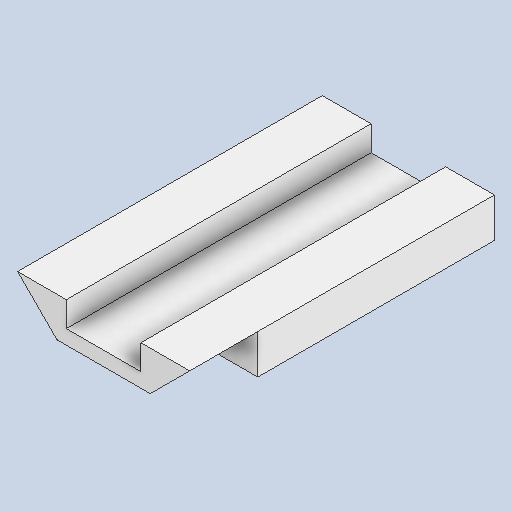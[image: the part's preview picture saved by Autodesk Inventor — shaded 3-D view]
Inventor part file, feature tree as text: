
AUTODESK INVENTOR PART (.ipt)
format: ipt  version: 2023 (Build 270158000, 158)  size: 268,800 bytes
history: native  units: mm
features: sketch x3, extrude x2, hole x1
ambient origin geometry x8: Origin, YZ Plane, XZ Plane, XY Plane, X Axis, Y Axis, Z Axis, Center Point
bodies: Solid1 (feature_tree)
feature tree (6):
  extrude  "Extrusion1"  TaperAngle=45.0deg  [1 undecoded]
  extrude  "Extrusion2"  Depth=10.4mm
  hole  "Hole1"  [1 undecoded]
  sketch  "Sketch1"  dims[d0=45.0deg d1=45.0deg]
  sketch  "Sketch2"  dims[d2=2.0mm d3=10.4mm]
  sketch  "Sketch3"  dims[d4=3.5mm d6=24.0mm d7=9.5mm d8=0.0mm d9=33.0mm d10=0.0mm d11=2.2mm d12=6.0mm d13=4.0mm d14=2.0mm d15=90.0deg d16=2.5mm d17=0.0mm d18=15.4mm d20=3.8mm d21=1.3mm]
note: 2 required parameter values undecoded (feature->parameter linkage not recoverable at this tier; creation-order binding heuristic only, values carry confidence <= 0.55)
